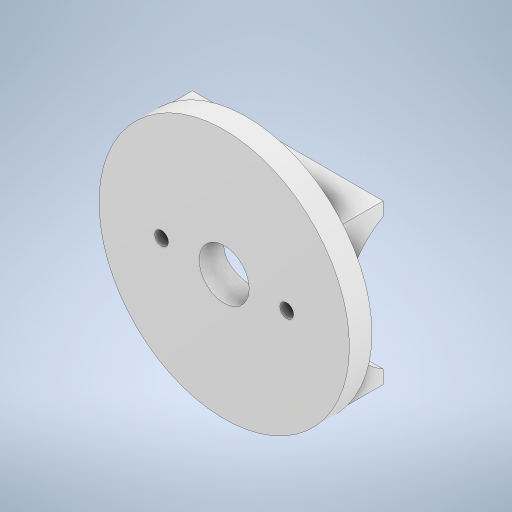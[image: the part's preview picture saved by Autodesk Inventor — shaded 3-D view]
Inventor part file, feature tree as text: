
AUTODESK INVENTOR PART (.ipt)
format: ipt  version: 2023 (Build 270158000, 158)  size: 266,752 bytes
history: native  units: in
note: dims shown in document units (in); Inventor stores cm internally (conversion verified against a paired STEP export)
features: sketch x4, extrude x3, hole x1
ambient origin geometry x8: Origin, YZ Plane, XZ Plane, XY Plane, X Axis, Y Axis, Z Axis, Center Point
bodies: Solid1 (feature_tree)
feature tree (8):
  extrude  "Extrusion1"  Depth=2.5in
  extrude  "Extrusion2"  Depth=1.0in
  extrude  "Extrusion3"  Depth=3.937in
  hole  "Hole1"  [1 undecoded]
  sketch  "Sketch1"  dims[d1=2.375in d3=2.5in]
  sketch  "Sketch2"  dims[d4=1.5748in d5=1.0in]
  sketch  "Sketch3"  dims[d6=3.0in d7=0.0in d8=3.937in]
  sketch  "Sketch5"  dims[d9=0.3543in d10=0.0in d11=0.7874in d12=0.0in d13=0.0in d14=0.2165in d15=0.3389in d16=0.0246in d17=0.426in d18=0.5906in d19=0.1693in d20=90.0deg d21=0.3543in d22=0.8108in d23=1.9685in d24=0.0394in d25=0.0394in d26=0.0394in d27=0.0059in d28=0.0098in d29=0.0148in d30=0.5635in d31=0.0295in d32=0.8108in d33=0.0025in d34=0.0295in d35=0.0148in]
note: 1 required parameter value undecoded (feature->parameter linkage not recoverable at this tier; creation-order binding heuristic only, values carry confidence <= 0.55)
